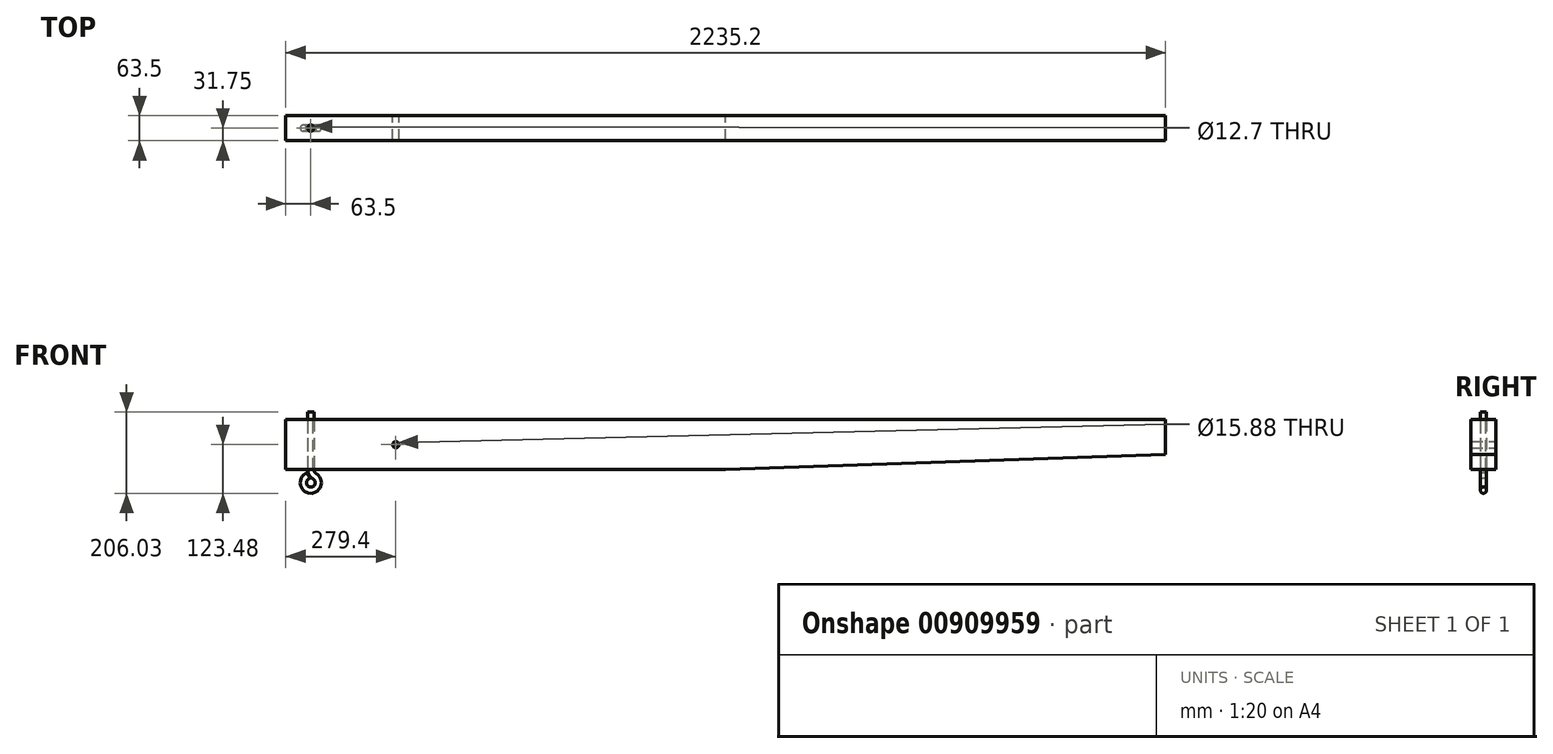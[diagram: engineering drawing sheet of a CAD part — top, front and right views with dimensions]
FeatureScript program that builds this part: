
annotation { "Feature Type Name" : "Feature", "Feature Type Description" : "" }
export const myFeature = defineFeature(function(context is Context, id is Id, definition is map)
    precondition{}
    {
        {
            var Q0;
            Q0=qCreatedBy(makeId("Front.planeOp"),FACE);
            var sketch = newSketch(context, id + "F0", { "sketchPlane" : qUnion([Q0])});
            skLineSegment(sketch, "E0.bottom", {"start": v(-279.4, 63.5) * mm, "end": v(1955.8, 63.5) * mm});
            skLineSegment(sketch, "E0.top", {"start": v(-279.4, -63.5) * mm, "end": v(838.2, -63.5) * mm});
            skLineSegment(sketch, "E0.left", {"start": v(-279.4, 63.5) * mm, "end": v(-279.4, -63.5) * mm});
            skLineSegment(sketch, "E0.right", {"start": v(1955.8, 63.5) * mm, "end": v(1955.8, -25.4) * mm});
            skLineSegment(sketch, "E1", {"start": v(-279.4, 0) * mm, "end": v(0, 0) * mm, "construction": true});
            skCircle(sketch, "E2", {"center": v(0, 0) * mm, "radius": 7.94 * mm});
            skLineSegment(sketch, "E3", {"start": v(838.2, -63.5) * mm, "end": v(1955.8, -25.4) * mm});
            skSolve(sketch);
        }
        {
            var Q0;
            Q0=makeQuery(id+"F0.imprint","IMPRINT",FACE,{"disambiguationData":[TD([[makeQuery(id+"F0.imprint","IMPRINT",EDGE,{"derivedFrom":sQuery(id+"F0.wireOp",EDGE,"E0.bottom")}),-1.0]])]});
            extrude(context, id + "F1", {"entities" : qUnion([Q0]), "depth" : 63.5 * mm, "offsetDistance" : 25 * mm, "symmetric" : true});
        }
        {
            var Q0;
            Q0=makeQuery(id+"F1.opExtrude","SWEPT_FACE",FACE,{"disambiguationData":[OSD([sQuery(id+"F0.wireOp",EDGE,"E0.bottom")])]});
            var sketch = newSketch(context, id + "F2", { "sketchPlane" : qUnion([Q0])});
            skCircle(sketch, "E4", {"center": v(-215.9, 0) * mm, "radius": 6.35 * mm});
            skSolve(sketch);
        }
        {
            var Q0;
            Q0=makeQuery(id+"F2.imprint","IMPRINT",FACE,{"disambiguationData":[TD([[makeQuery(id+"F2.imprint","IMPRINT",EDGE,{"derivedFrom":sQuery(id+"F2.wireOp",EDGE,"E4")}),1.0]])]});
            extrude(context, id + "F3", {"entities" : qUnion([Q0]), "operationType" : NewBodyOperationType.REMOVE, "endBound" : BoundingType.THROUGH_ALL, "oppositeDirection" : true, "depth" : 25 * mm, "offsetDistance" : 25 * mm});
        }
        {
            var Q0;
            Q0=qCreatedBy(makeId("Front.planeOp"),FACE);
            var sketch = newSketch(context, id + "F4", { "sketchPlane" : qUnion([Q0])});
            skLineSegment(sketch, "E5", {"start": v(-215.9, 82.55) * mm, "end": v(-215.9, -63.5) * mm});
            skArc(sketch, "E6", {"start": v(-225.42, -80) * mm, "mid": v(-215.9, -115.55) * mm, "end": v(-206.37, -80) * mm});
            skArc(sketch, "E7", {"start": v(-215.9, -63.5) * mm, "mid": v(-213.35, -73.03) * mm, "end": v(-206.37, -80) * mm});
            skLineSegment(sketch, "E8", {"start": v(-225.42, -80) * mm, "end": v(-222, -78.02) * mm});
            skSolve(sketch);
        }
        {
            var Q0;
            Q0=sQuery(id+"F4.wireOp",VERTEX,"E5.start");
            var Q1;
            Q1=sQuery(id+"F4.wireOp",EDGE,"E5");
            cPlane(context, id + "F5", {"entities" : qUnion([Q0, Q1]), "cplaneType" : CPlaneType.LINE_POINT, "offset" : 25 * mm, "width" : 150 * mm, "height" : 150 * mm});
        }
        {
            var Q0;
            Q0=qCreatedBy(id+"F5.planeOp",FACE);
            var sketch = newSketch(context, id + "F6", { "sketchPlane" : qUnion([Q0])});
            skCircle(sketch, "E9", {"center": v(-215.9, 0) * mm, "radius": 7.94 * mm});
            skSolve(sketch);
        }
        {
            var Q0;
            Q0=makeQuery(id+"F6.imprint","IMPRINT",FACE,{"disambiguationData":[TD([[makeQuery(id+"F6.imprint","IMPRINT",EDGE,{"derivedFrom":sQuery(id+"F6.wireOp",EDGE,"E9")}),1.0]])]});
            var Q1;
            Q1=sQuery(id+"F4.wireOp",EDGE,"E5");
            var Q2;
            Q2=sQuery(id+"F4.wireOp",EDGE,"E7");
            var Q3;
            Q3=sQuery(id+"F4.wireOp",EDGE,"E6");
            var Q4;
            Q4=sQuery(id+"F4.wireOp",EDGE,"E8");
            sweep(context, id + "F7", {"profiles" : qUnion([Q0]), "path" : qUnion([Q1, Q2, Q3, Q4])});
        }
    });
